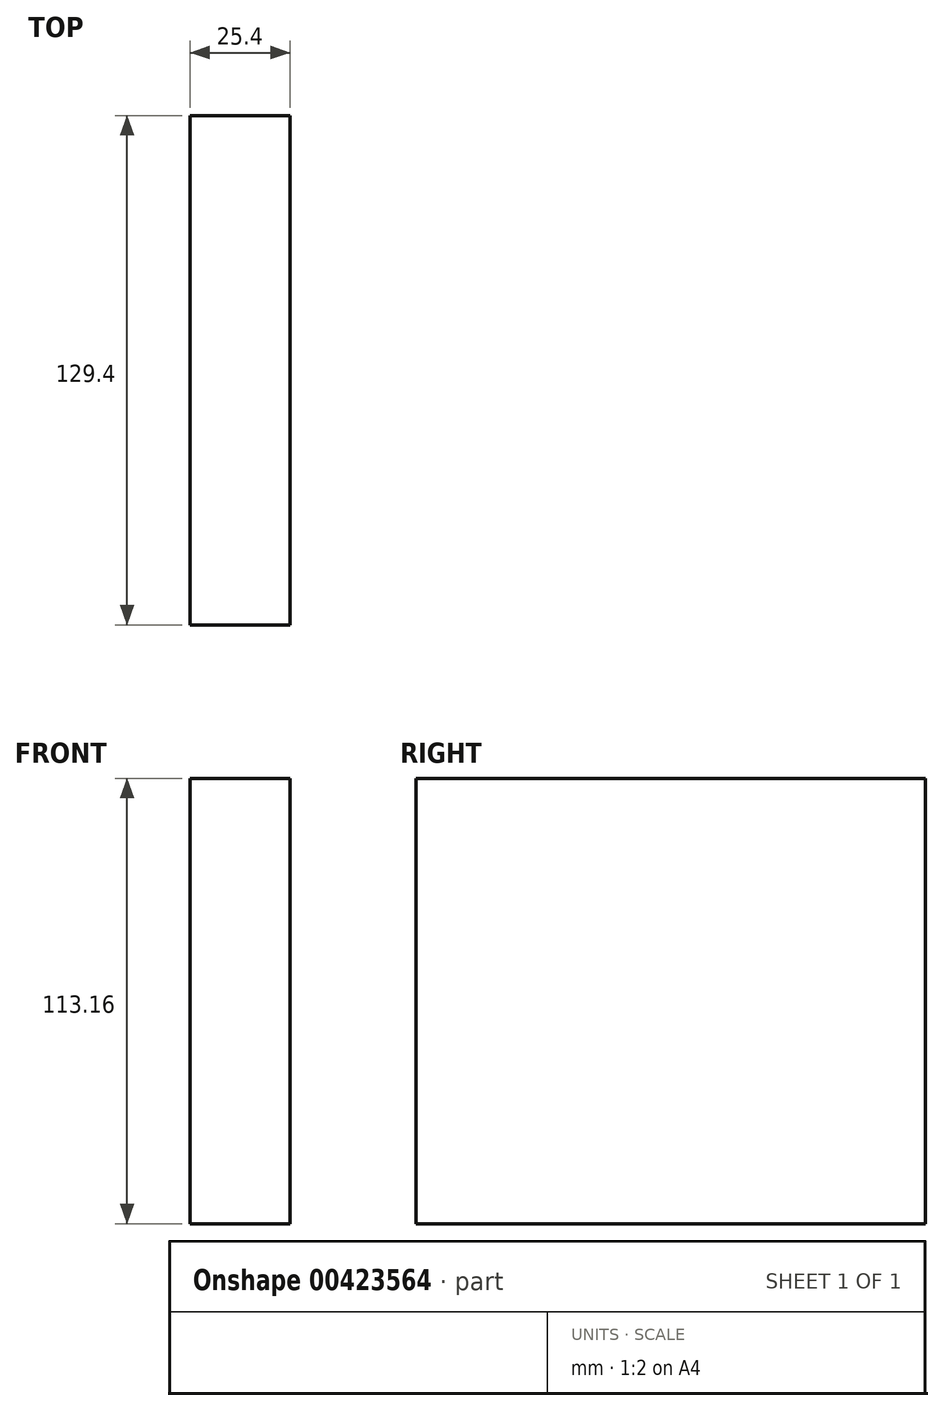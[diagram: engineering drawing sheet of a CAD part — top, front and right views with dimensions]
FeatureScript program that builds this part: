
annotation { "Feature Type Name" : "Feature", "Feature Type Description" : "" }
export const myFeature = defineFeature(function(context is Context, id is Id, definition is map)
    precondition{}
    {
        {
            var Q0;
            Q0=qCreatedBy(makeId("Right.planeOp"),FACE);
            var sketch = newSketch(context, id + "F0", { "sketchPlane" : qUnion([Q0])});
            skLineSegment(sketch, "E0.bottom", {"start": v(-56.83, 55.93) * mm, "end": v(72.57, 55.93) * mm});
            skLineSegment(sketch, "E0.top", {"start": v(-56.83, -57.23) * mm, "end": v(72.57, -57.23) * mm});
            skLineSegment(sketch, "E0.left", {"start": v(-56.83, 55.93) * mm, "end": v(-56.83, -57.23) * mm});
            skLineSegment(sketch, "E0.right", {"start": v(72.57, 55.93) * mm, "end": v(72.57, -57.23) * mm});
            skSolve(sketch);
        }
        {
            var Q0;
            Q0 = qSketchRegion(id + "F0", true);
            var Q1;
            Q1=makeQuery(id+"F0.imprint","IMPRINT",FACE,{"disambiguationData":[TD([[makeQuery(id+"F0.imprint","IMPRINT",EDGE,{"derivedFrom":sQuery(id+"F0.wireOp",EDGE,"E0.bottom")}),-1.0]])]});
            extrude(context, id + "F1", {"entities" : qUnion([Q0, Q1]), "depth" : 25.4 * mm});
        }
    });
